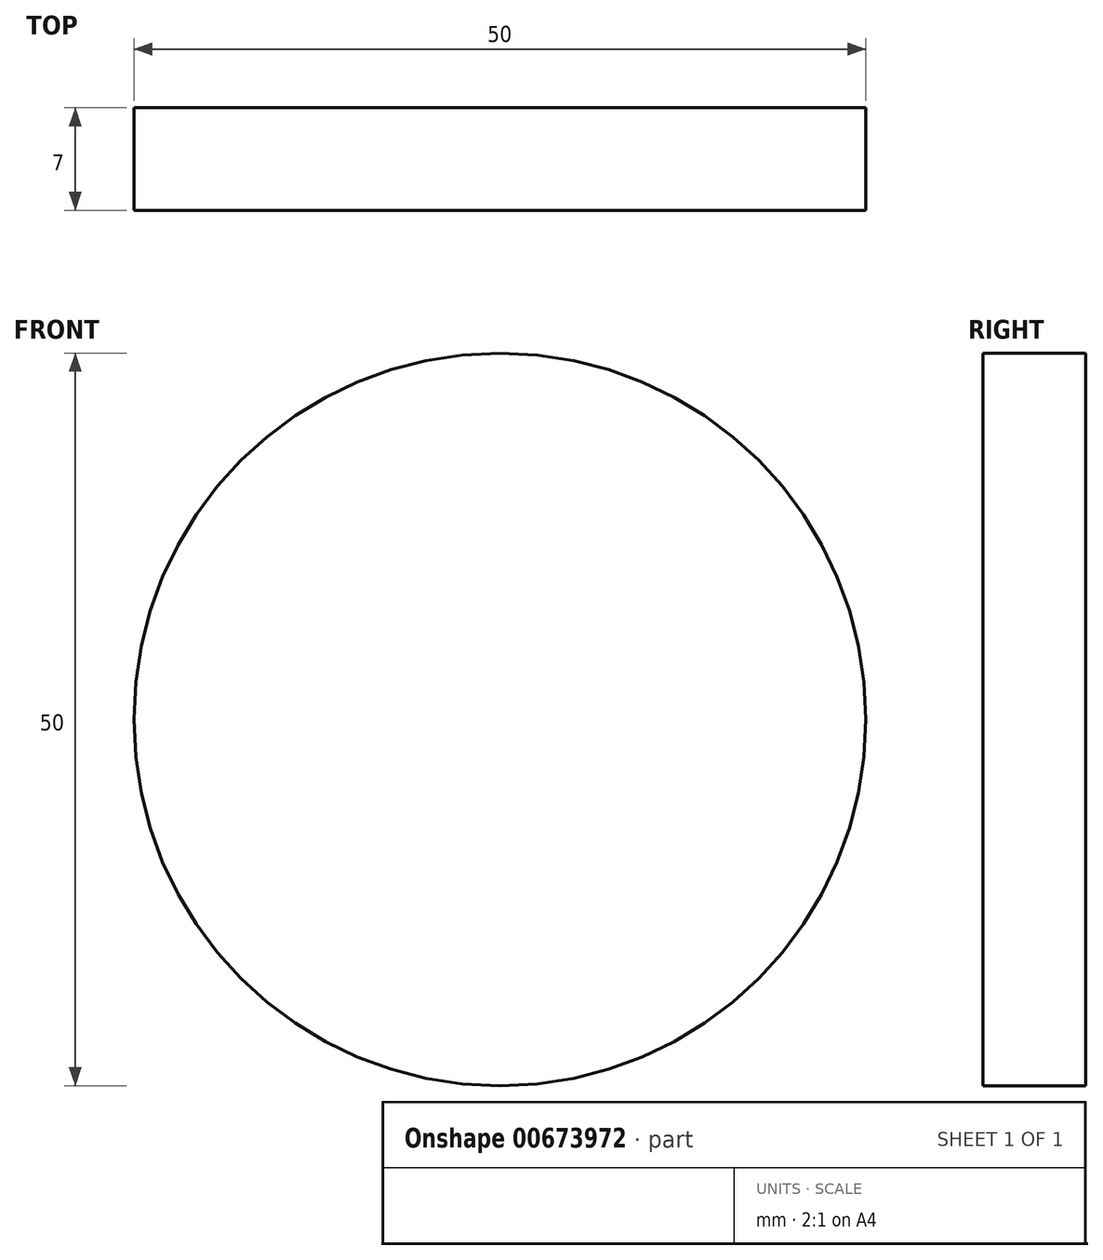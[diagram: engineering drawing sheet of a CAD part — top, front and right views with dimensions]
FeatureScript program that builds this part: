
annotation { "Feature Type Name" : "Feature", "Feature Type Description" : "" }
export const myFeature = defineFeature(function(context is Context, id is Id, definition is map)
    precondition{}
    {
        {
            var Q0;
            Q0=qCreatedBy(makeId("Front.planeOp"),FACE);
            var sketch = newSketch(context, id + "F0", { "sketchPlane" : qUnion([Q0])});
            skCircle(sketch, "E0", {"center": v(0, 0) * mm, "radius": 25 * mm});
            skSolve(sketch);
        }
        {
            var Q0;
            Q0=makeQuery(id+"F0.imprint","IMPRINT",FACE,{"disambiguationData":[TD([[makeQuery(id+"F0.imprint","IMPRINT",EDGE,{"derivedFrom":sQuery(id+"F0.wireOp",EDGE,"E0")}),1.0]])]});
            extrude(context, id + "F1", {"entities" : qUnion([Q0]), "depth" : 7 * mm, "offsetDistance" : 25 * mm});
        }
    });
